# Revit family: NBS_ConceptCubicleSystems_PnlCbclSym_LittleOnes
name_source: partatom
category: Specialty Equipment
units: mm (PartAtom-declared; Revit-internal decimal feet)

## family parameters
Always vertical = Yes
Cut with Voids When Loaded = No
Part Type = Normal
Room Calculation Point = No
Round Connector Dimension = Use Diameter
Shared = No
Work Plane-Based = No

## types (5) — shared parameters
Application = Designed for nursery washrooms
AssetType = Fixed
Category = Ss_25_12_60_60:Panel cubicle systems
Color = Rainbow design as standard
Description = Toilet cubicle designed for nusery application
DoorLeafMaterial = NBS_ConceptCubicleSystems_C062_Capucine-Red
DoorLeafUndercut = 150 mm
DurationUnit = year
Features = Manufactured from 12-13 mm compact grade laminate, easy to clean and robust, bespoke images can be printed onto the pilasters for additional cost
FittingMaterial = NBS_ConceptCubicleSystems_SatinAnodisedAluminium
Fittings = Colourful, powder coated fittings
IfcExportAs = IfcFurnitureType
IfcExportType = USERDEFINED
IsBuiltIn = Yes
ManufacturerName = Concept Cubicle Systems
ManufacturerURL = www.conceptcubiclesystems.co.uk
Material = Compact Grade Laminate
ModelReference = Little Ones Toilet Cubicles
NBSCertification = www.nationalbimlibrary.com/cert/rokubya4
NBSDescription = Panel cubicle system
NBSReference = 25-05-60/160
PanelSupports = 150 mm
PanelThickness = 13 mm
Panels = 12 mm compact grade laminate
PartitionMaterial = NBS_ConceptCubicleSystems_C062_Capucine-Red
PartitionUndercut = 150 mm
PilasterMaterial = NBS_ConceptCubicleSystems_SatinAnodisedAluminium
ProductInformation = https://www.conceptcubiclesystems.co.uk
Size = 1500 x 1200 mm
Status = UNSET
Style = Cubicle
SystemManufacturer = Concept Cubicle Systems
Uniclass2015Code = Ss_25_12_60_60
Uniclass2015Title = Panel cubicle systems
Uniclass2015Version = Systems v1.17
Version = 3
WarrantyDurationUnit = year

## per-type parameters (varying)
| type | BIMObjectName | HasPartitionLeft | HasPartitionRight | HasPilasterLeft | HasPilasterLeftWall | HasPilasterRight | HasPilasterRightWall | IsEndCubicle | IsFirstCubicle | IsMiddleCubicle | IsSingleCubicle | IsWallEndEndCubicle | IsWallEndFirstCubicle | IsWallToWallSingleCubicle | Name |
| FirstOrSingleCubicle | NBS_ConceptCubicleSystems_PanelCubicleSystem_LittleOnes_FirstOrSingleCubicle | Yes | Yes | Yes | No | Yes | No | No | Yes | No | Yes | No | No | No | PanelCubicleSystem_LittleOnes_FirstOrSingleCubicle_ConceptCubicleSystems |
| WallToWallSingleCubicle | NBS_ConceptCubicleSystems_PanelCubicleSystem_LittleOnes_WallToWallSingleCubicle | No | No | No | Yes | No | Yes | No | No | No | No | No | No | Yes | PanelCubicleSystem_LittleOnes_WallToWallSingleCubicle_ConceptCubicleSystems |
| WallEndFirstCubicle | NBS_ConceptCubicleSystems_PanelCubicleSystem_LittleOnes_WallEndFirstCubicle | No | Yes | No | Yes | Yes | No | No | No | No | No | No | Yes | No | PanelCubicleSystem_LittleOnes_WallEndFirstCubicle_ConceptCubicleSystems |
| MiddleOrEndCubicle | NBS_ConceptCubicleSystems_PanelCubicleSystem_LittleOnes_MiddleOrEndCubicle | No | Yes | No | No | Yes | No | Yes | No | Yes | No | No | No | No | PanelCubicleSystem_LittleOnes_MiddleOrEndCubicle_ConceptCubicleSystems |
| WallEndEndCubicle | NBS_ConceptCubicleSystems_PanelCubicleSystem_LittleOnes_WallEndEndCubicle | No | No | No | No | No | Yes | No | No | No | No | Yes | No | No | PanelCubicleSystem_LittleOnes_WallEndEndCubicle_ConceptCubicleSystems |

## geometry (parser evidence)
native form markers: Sweep x7
no freeform markers — native parametric forms only
